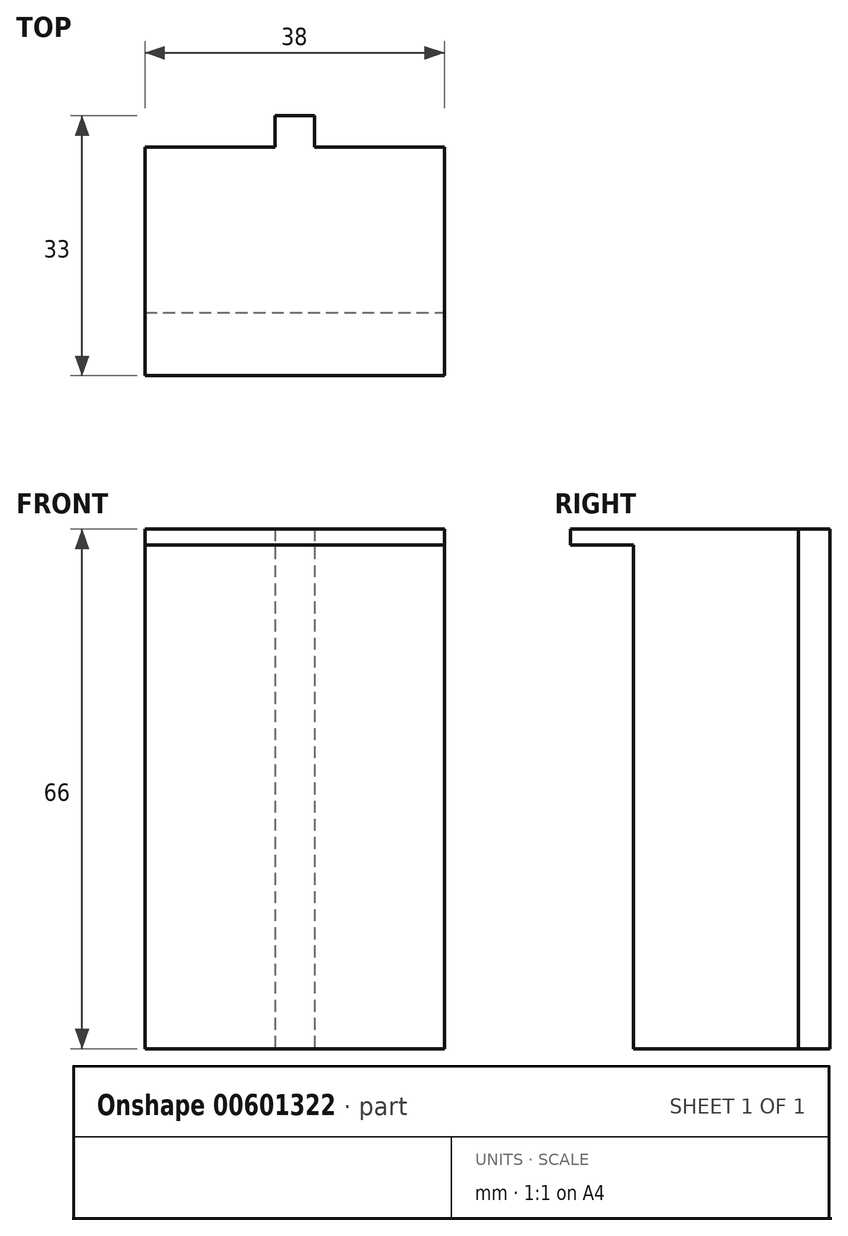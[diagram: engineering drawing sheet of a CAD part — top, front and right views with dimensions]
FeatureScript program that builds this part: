
annotation { "Feature Type Name" : "Feature", "Feature Type Description" : "" }
export const myFeature = defineFeature(function(context is Context, id is Id, definition is map)
    precondition{}
    {
        {
            var Q0;
            Q0=qCreatedBy(makeId("Front.planeOp"),FACE);
            var sketch = newSketch(context, id + "F0", { "sketchPlane" : qUnion([Q0])});
            skLineSegment(sketch, "E0.bottom", {"start": v(-54, 0) * mm, "end": v(-16, 0) * mm});
            skLineSegment(sketch, "E0.top", {"start": v(-54, -66) * mm, "end": v(-16, -66) * mm});
            skLineSegment(sketch, "E0.left", {"start": v(-54, 0) * mm, "end": v(-54, -66) * mm});
            skLineSegment(sketch, "E0.right", {"start": v(-16, 0) * mm, "end": v(-16, -66) * mm});
            skLineSegment(sketch, "E1", {"start": v(-35, 0) * mm, "end": v(-35, -66) * mm, "construction": true});
            skLineSegment(sketch, "E2.0", {"start": v(-32.5, 0) * mm, "end": v(-32.5, -66) * mm});
            skLineSegment(sketch, "E3.0", {"start": v(-37.5, 0) * mm, "end": v(-37.5, -66) * mm});
            skLineSegment(sketch, "E4", {"start": v(-37.5, 0) * mm, "end": v(-32.5, 0) * mm});
            skLineSegment(sketch, "E5", {"start": v(-37.5, -66) * mm, "end": v(-32.5, -66) * mm});
            skSolve(sketch);
        }
        {
            var Q0;
            Q0=makeQuery(id+"F0.imprint","IMPRINT",FACE,{"disambiguationData":[TD([[makeQuery(id+"F0.imprint","IMPRINT",EDGE,{"derivedFrom":sQuery(id+"F0.wireOp",EDGE,"E2.0")}),-1.0]])]});
            var Q1;
            {var subQ0=sQuery(id+"F0.wireOp",EDGE,"E0.left");Q1=makeQuery(id+"F0.imprint","IMPRINT",FACE,{"disambiguationData":[TD([[makeQuery(id+"F0.imprint","IMPRINT",EDGE,{"derivedFrom":subQ0}),1.0]])]});}
            var Q2;
            {var subQ0=sQuery(id+"F0.wireOp",EDGE,"E2.0");Q2=makeQuery(id+"F0.imprint","IMPRINT",FACE,{"disambiguationData":[TD([[makeQuery(id+"F0.imprint","IMPRINT",EDGE,{"derivedFrom":subQ0}),1.0]])]});}
            var Q3;
            {var subQ0=sQuery(id+"F0.wireOp",EDGE,"745ce9f3-55c7-40ce-afe4-fad1f71680130.MirrorCS");Q3=makeQuery(id+"F0.imprint","IMPRINT",FACE,{"disambiguationData":[TD([[makeQuery(id+"F0.imprint","IMPRINT",EDGE,{"derivedFrom":subQ0}),1.0]])]});}
            var Q4;
            {var subQ0=sQuery(id+"F0.wireOp",EDGE,"E0.right");Q4=makeQuery(id+"F0.imprint","IMPRINT",FACE,{"disambiguationData":[TD([[makeQuery(id+"F0.imprint","IMPRINT",EDGE,{"derivedFrom":subQ0}),-1.0]])]});}
            extrude(context, id + "F1", {"entities" : qUnion([Q0, Q1, Q2, Q3, Q4]), "depth" : 21 * mm, "offsetDistance" : 25 * mm});
        }
        {
            var Q0;
            {var subQ0=sQuery(id+"F0.wireOp",EDGE,"745ce9f3-55c7-40ce-afe4-fad1f71680130.MirrorCS");Q0=makeQuery(id+"F0.imprint","IMPRINT",FACE,{"disambiguationData":[TD([[makeQuery(id+"F0.imprint","IMPRINT",EDGE,{"derivedFrom":subQ0}),1.0]])]});}
            var Q1;
            Q1=makeQuery(id+"F0.imprint","IMPRINT",FACE,{"disambiguationData":[TD([[makeQuery(id+"F0.imprint","IMPRINT",EDGE,{"derivedFrom":sQuery(id+"F0.wireOp",EDGE,"E2.0")}),-1.0]])]});
            extrude(context, id + "F2", {"entities" : qUnion([Q0, Q1]), "operationType" : NewBodyOperationType.ADD, "oppositeDirection" : true, "depth" : 4 * mm, "offsetDistance" : 25 * mm});
        }
        {
            var Q0;
            Q0=makeQuery(id+"F1.opExtrude","CAP_FACE",FACE,{"disambiguationData":[OSD([sQuery(id+"F0.wireOp",EDGE,"E0.bottom"),sQuery(id+"F0.wireOp",EDGE,"E0.top"),sQuery(id+"F0.wireOp",EDGE,"E0.left"),sQuery(id+"F0.wireOp",EDGE,"E0.right"),sQuery(id+"F0.wireOp",EDGE,"E4"),sQuery(id+"F0.wireOp",EDGE,"E5")])],"isStart":false});
            var sketch = newSketch(context, id + "F3", { "sketchPlane" : qUnion([Q0])});
            skLineSegment(sketch, "E6.bottom", {"start": v(-54, 0) * mm, "end": v(-16, 0) * mm});
            skLineSegment(sketch, "E6.top", {"start": v(-54, -2) * mm, "end": v(-16, -2) * mm});
            skLineSegment(sketch, "E6.left", {"start": v(-54, 0) * mm, "end": v(-54, -2) * mm});
            skLineSegment(sketch, "E6.right", {"start": v(-16, 0) * mm, "end": v(-16, -2) * mm});
            skSolve(sketch);
        }
        {
            var Q0;
            Q0=qSketchRegion(id+"F3",true);
            extrude(context, id + "F4", {"entities" : qUnion([Q0]), "operationType" : NewBodyOperationType.ADD, "depth" : 8 * mm, "offsetDistance" : 25 * mm});
        }
    });
